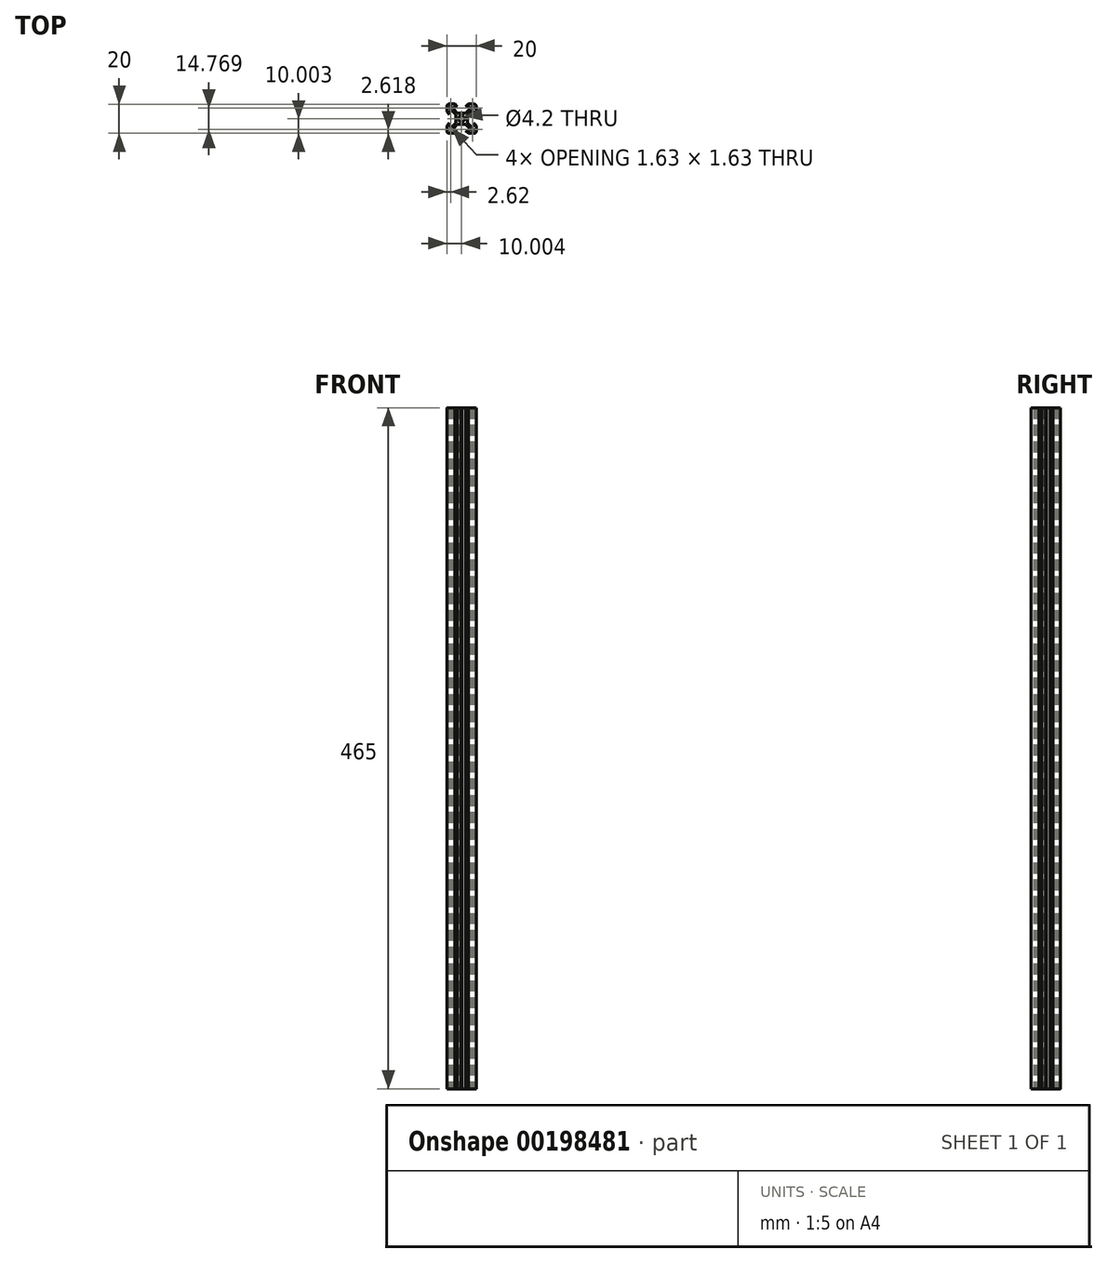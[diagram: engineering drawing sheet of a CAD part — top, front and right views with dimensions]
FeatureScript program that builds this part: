
annotation { "Feature Type Name" : "Feature", "Feature Type Description" : "" }
export const myFeature = defineFeature(function(context is Context, id is Id, definition is map)
    precondition{}
    {
        {
            var Q0;
            Q0=qCreatedBy(makeId("Top.planeOp"),FACE);
            var sketch = newSketch(context, id + "F0", { "sketchPlane" : qUnion([Q0])});
            skLineSegment(sketch, "E0", {"start": v(19.2, 3.45) * mm, "end": v(19.2, -0.4) * mm});
            skLineSegment(sketch, "E1", {"start": v(17.7, -15.05) * mm, "end": v(13.83, -15.05) * mm});
            skLineSegment(sketch, "E2", {"start": v(-0.8, -13.55) * mm, "end": v(-0.8, -9.69) * mm});
            skLineSegment(sketch, "E3", {"start": v(0.7, 4.95) * mm, "end": v(4.55, 4.95) * mm});
            skLineSegment(sketch, "E4.0", {"start": v(3.7, 3.15) * mm, "end": v(6.35, 3.15) * mm});
            skLineSegment(sketch, "E4.1", {"start": v(1, -10.55) * mm, "end": v(1, -7.89) * mm});
            skLineSegment(sketch, "E4.2", {"start": v(14.7, -13.25) * mm, "end": v(12.03, -13.25) * mm});
            skLineSegment(sketch, "E4.3", {"start": v(17.4, 0.45) * mm, "end": v(17.4, -2.2) * mm});
            skLineSegment(sketch, "E5.trimOffspring", {"start": v(13.83, 4.95) * mm, "end": v(17.7, 4.95) * mm});
            skPoint(sketch, "E6.start.orphan", {"position": v(9.2, 4.95) * mm});
            skLineSegment(sketch, "E7", {"start": v(6.35, 3.15) * mm, "end": v(4.55, 4.95) * mm});
            skLineSegment(sketch, "E8.trimOffspring", {"start": v(12.03, 3.15) * mm, "end": v(14.7, 3.15) * mm});
            skLineSegment(sketch, "E9.MirrorCS", {"start": v(12.03, 3.15) * mm, "end": v(13.83, 4.95) * mm});
            skLineSegment(sketch, "E10.MirrorCS", {"start": v(12.03, -13.25) * mm, "end": v(13.83, -15.05) * mm});
            skLineSegment(sketch, "E11.MirrorCS", {"start": v(6.35, -13.25) * mm, "end": v(4.55, -15.05) * mm});
            skLineSegment(sketch, "E12.trimOffspring", {"start": v(6.35, -13.25) * mm, "end": v(3.7, -13.25) * mm});
            skLineSegment(sketch, "E13.trimOffspring", {"start": v(4.55, -15.05) * mm, "end": v(0.7, -15.05) * mm});
            skLineSegment(sketch, "E14", {"start": v(1, -2.2) * mm, "end": v(-0.8, -0.4) * mm});
            skLineSegment(sketch, "E15", {"start": v(1, -7.89) * mm, "end": v(-0.8, -9.69) * mm});
            skLineSegment(sketch, "E16.trimOffspring", {"start": v(-0.8, -0.4) * mm, "end": v(-0.8, 3.45) * mm});
            skLineSegment(sketch, "E17.trimOffspring", {"start": v(1, -2.2) * mm, "end": v(1, 0.45) * mm});
            skLineSegment(sketch, "E18.MirrorCS", {"start": v(17.4, -2.2) * mm, "end": v(19.2, -0.4) * mm});
            skLineSegment(sketch, "E19.MirrorCS", {"start": v(17.4, -7.89) * mm, "end": v(19.2, -9.69) * mm});
            skLineSegment(sketch, "E20.trimOffspring", {"start": v(17.4, -7.89) * mm, "end": v(17.4, -10.55) * mm});
            skLineSegment(sketch, "E21.trimOffspring", {"start": v(19.2, -9.69) * mm, "end": v(19.2, -13.55) * mm});
            skCircle(sketch, "E22", {"center": v(9.2, -5.05) * mm, "radius": 2.1 * mm});
            skLineSegment(sketch, "E23", {"start": v(2.63, 0.45) * mm, "end": v(5.3, -2.2) * mm});
            skLineSegment(sketch, "E24", {"start": v(3.7, 1.51) * mm, "end": v(6.35, -1.15) * mm});
            skLineSegment(sketch, "E25", {"start": v(3.7, 1.51) * mm, "end": v(3.7, 3.15) * mm});
            skLineSegment(sketch, "E26", {"start": v(2.63, 0.45) * mm, "end": v(1, 0.45) * mm});
            skLineSegment(sketch, "E27", {"start": v(15.75, 0.45) * mm, "end": v(13.1, -2.2) * mm});
            skLineSegment(sketch, "E28", {"start": v(14.7, 1.51) * mm, "end": v(12.03, -1.15) * mm});
            skLineSegment(sketch, "E29", {"start": v(2.63, -10.55) * mm, "end": v(1, -10.55) * mm});
            skLineSegment(sketch, "E30", {"start": v(3.7, -11.6) * mm, "end": v(3.7, -13.25) * mm});
            skLineSegment(sketch, "E31", {"start": v(14.7, 1.51) * mm, "end": v(14.7, 3.15) * mm});
            skLineSegment(sketch, "E32", {"start": v(15.75, 0.45) * mm, "end": v(17.4, 0.45) * mm});
            skLineSegment(sketch, "E33", {"start": v(14.7, -11.6) * mm, "end": v(14.7, -13.25) * mm});
            skLineSegment(sketch, "E34", {"start": v(15.75, -10.55) * mm, "end": v(17.4, -10.55) * mm});
            skLineSegment(sketch, "E35.trimOffspring", {"start": v(12.03, -8.95) * mm, "end": v(14.7, -11.6) * mm});
            skLineSegment(sketch, "E36.trimOffspring", {"start": v(6.35, -8.95) * mm, "end": v(3.7, -11.6) * mm});
            skLineSegment(sketch, "E37.trimOffspring", {"start": v(5.3, -7.89) * mm, "end": v(2.63, -10.55) * mm});
            skLineSegment(sketch, "E38.trimOffspring", {"start": v(13.1, -7.89) * mm, "end": v(15.75, -10.55) * mm});
            skLineSegment(sketch, "E39", {"start": v(5.3, -7.89) * mm, "end": v(5.3, -5.3) * mm});
            skLineSegment(sketch, "E40", {"start": v(6.35, -1.15) * mm, "end": v(8.94, -1.15) * mm});
            skLineSegment(sketch, "E41", {"start": v(6.35, -8.95) * mm, "end": v(8.94, -8.95) * mm});
            skLineSegment(sketch, "E42", {"start": v(13.1, -2.2) * mm, "end": v(13.1, -4.8) * mm});
            skLineSegment(sketch, "E43", {"start": v(1, 1.52) * mm, "end": v(1, 3.15) * mm});
            skLineSegment(sketch, "E44", {"start": v(2.63, 3.15) * mm, "end": v(1, 3.15) * mm});
            skLineSegment(sketch, "E45", {"start": v(1, 1.52) * mm, "end": v(1.56, 1.52) * mm});
            skLineSegment(sketch, "E46", {"start": v(2.63, 3.15) * mm, "end": v(2.63, 2.58) * mm});
            skLineSegment(sketch, "E47", {"start": v(1.56, 1.52) * mm, "end": v(2.63, 2.58) * mm});
            skLineSegment(sketch, "E48.MirrorCS", {"start": v(15.76, 3.15) * mm, "end": v(17.4, 3.15) * mm});
            skLineSegment(sketch, "E49.MirrorCS", {"start": v(17.4, 1.52) * mm, "end": v(17.4, 3.15) * mm});
            skLineSegment(sketch, "E50.MirrorCS", {"start": v(17.4, 1.52) * mm, "end": v(16.82, 1.52) * mm});
            skLineSegment(sketch, "E51.MirrorCS", {"start": v(16.82, 1.52) * mm, "end": v(15.76, 2.58) * mm});
            skLineSegment(sketch, "E52.MirrorCS", {"start": v(15.76, 3.15) * mm, "end": v(15.76, 2.58) * mm});
            skLineSegment(sketch, "E53.MirrorCS", {"start": v(15.76, -13.25) * mm, "end": v(15.76, -12.68) * mm});
            skLineSegment(sketch, "E54.MirrorCS", {"start": v(17.4, -11.62) * mm, "end": v(16.82, -11.62) * mm});
            skLineSegment(sketch, "E55.MirrorCS", {"start": v(16.82, -11.62) * mm, "end": v(15.76, -12.68) * mm});
            skLineSegment(sketch, "E56.MirrorCS", {"start": v(15.76, -13.25) * mm, "end": v(17.4, -13.25) * mm});
            skLineSegment(sketch, "E57.MirrorCS", {"start": v(17.4, -11.62) * mm, "end": v(17.4, -13.25) * mm});
            skLineSegment(sketch, "E58.MirrorCS", {"start": v(2.63, -13.25) * mm, "end": v(1, -13.25) * mm});
            skLineSegment(sketch, "E59.MirrorCS", {"start": v(1, -11.62) * mm, "end": v(1.56, -11.62) * mm});
            skLineSegment(sketch, "E60.MirrorCS", {"start": v(1, -11.62) * mm, "end": v(1, -13.25) * mm});
            skLineSegment(sketch, "E61.MirrorCS", {"start": v(1.56, -11.62) * mm, "end": v(2.63, -12.68) * mm});
            skLineSegment(sketch, "E62.MirrorCS", {"start": v(2.63, -13.25) * mm, "end": v(2.63, -12.68) * mm});
            skPoint(sketch, "E63.visualSharp", {"position": v(-0.8, 4.95) * mm});
            skArc(sketch, "E63.filletArc", {"start": v(0.7, 4.95) * mm, "mid": v(-0.37, 4.51) * mm, "end": v(-0.8, 3.45) * mm});
            skPoint(sketch, "E64.visualSharp", {"position": v(19.2, 4.95) * mm});
            skArc(sketch, "E64.filletArc", {"start": v(19.2, 3.45) * mm, "mid": v(18.76, 4.51) * mm, "end": v(17.7, 4.95) * mm});
            skPoint(sketch, "E65.visualSharp", {"position": v(19.2, -15.05) * mm});
            skArc(sketch, "E65.filletArc", {"start": v(17.7, -15.05) * mm, "mid": v(18.76, -14.6) * mm, "end": v(19.2, -13.55) * mm});
            skPoint(sketch, "E66.visualSharp", {"position": v(-0.8, -15.05) * mm});
            skArc(sketch, "E66.filletArc", {"start": v(-0.8, -13.55) * mm, "mid": v(-0.37, -14.6) * mm, "end": v(0.7, -15.05) * mm});
            skLineSegment(sketch, "E67", {"start": v(5.54, -5.05) * mm, "end": v(5.3, -4.8) * mm});
            skLineSegment(sketch, "E68.MirrorCS", {"start": v(5.54, -5.05) * mm, "end": v(5.3, -5.3) * mm});
            skLineSegment(sketch, "E69.trimOffspring", {"start": v(5.3, -4.8) * mm, "end": v(5.3, -2.2) * mm});
            skLineSegment(sketch, "E70.MirrorCS", {"start": v(12.85, -5.05) * mm, "end": v(13.1, -4.8) * mm});
            skLineSegment(sketch, "E71.MirrorCS", {"start": v(12.85, -5.05) * mm, "end": v(13.1, -5.3) * mm});
            skLineSegment(sketch, "E72", {"start": v(9.2, -8.7) * mm, "end": v(9.44, -8.95) * mm});
            skLineSegment(sketch, "E73.MirrorCS", {"start": v(9.2, -8.7) * mm, "end": v(8.94, -8.95) * mm});
            skLineSegment(sketch, "E74.trimOffspring", {"start": v(9.44, -8.95) * mm, "end": v(12.03, -8.95) * mm});
            skLineSegment(sketch, "E75.trimOffspring", {"start": v(13.1, -5.3) * mm, "end": v(13.1, -7.89) * mm});
            skLineSegment(sketch, "E76.MirrorCS", {"start": v(9.2, -1.4) * mm, "end": v(8.94, -1.15) * mm});
            skLineSegment(sketch, "E77.MirrorCS", {"start": v(9.2, -1.4) * mm, "end": v(9.44, -1.15) * mm});
            skLineSegment(sketch, "E78.trimOffspring", {"start": v(9.44, -1.15) * mm, "end": v(12.03, -1.15) * mm});
            skSolve(sketch);
        }
        {
            var Q0;
            Q0 = qSketchRegion(id + "F0", true);
            extrude(context, id + "F1", {"entities" : qUnion([Q0]), "depth" : (505 - 40) * mm});
        }
    });
